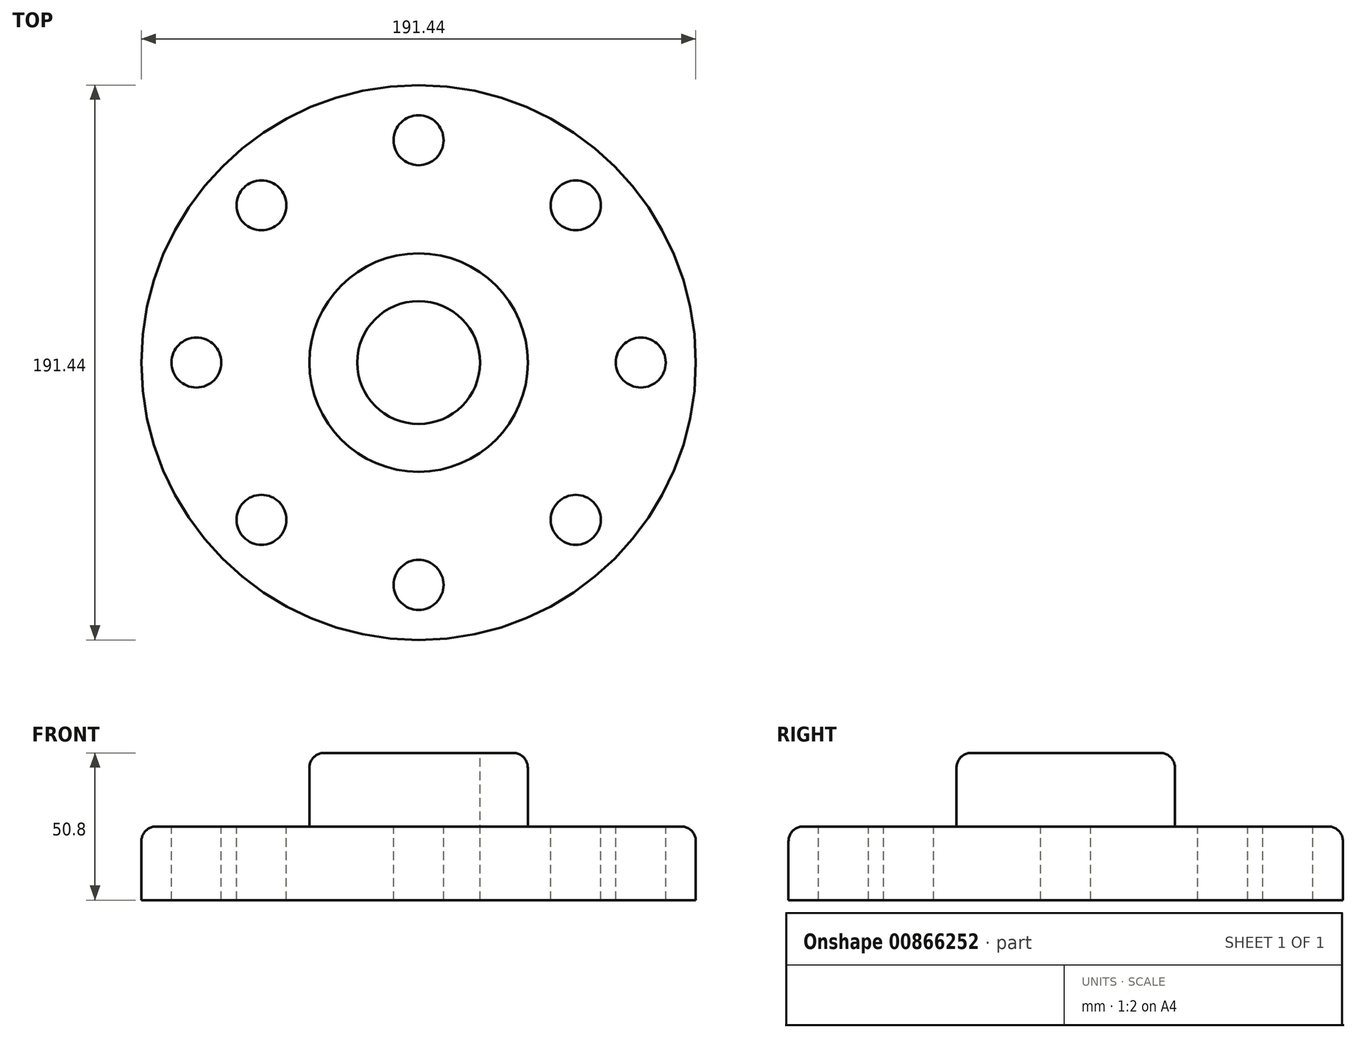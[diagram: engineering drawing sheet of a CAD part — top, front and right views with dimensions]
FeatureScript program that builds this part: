
annotation { "Feature Type Name" : "Feature", "Feature Type Description" : "" }
export const myFeature = defineFeature(function(context is Context, id is Id, definition is map)
    precondition{}
    {
        {
            var Q0;
            Q0=qCreatedBy(makeId("Top.planeOp"),FACE);
            var sketch = newSketch(context, id + "F0", { "sketchPlane" : qUnion([Q0])});
            skCircle(sketch, "E0", {"center": v(0, 0) * mm, "radius": 95.72 * mm});
            skCircle(sketch, "E1", {"center": v(0, 0) * mm, "radius": 37.7 * mm});
            skSolve(sketch);
        }
        {
            var Q0;
            Q0=makeQuery(id+"F0.imprint","IMPRINT",FACE,{"disambiguationData":[TD([[makeQuery(id+"F0.imprint","IMPRINT",EDGE,{"derivedFrom":sQuery(id+"F0.wireOp",EDGE,"E1")}),1.0]])]});
            extrude(context, id + "F1", {"entities" : qUnion([Q0]), "depth" : 50.8 * mm, "offsetDistance" : 25.4 * mm});
        }
        {
            var Q0;
            Q0 = qSketchRegion(id + "F0", true);
            extrude(context, id + "F2", {"entities" : qUnion([Q0]), "operationType" : NewBodyOperationType.ADD, "depth" : 25.4 * mm, "offsetDistance" : 25.4 * mm});
        }
        {
            var Q0;
            Q0=makeQuery(id+"F2.opExtrude","CAP_FACE",FACE,{"disambiguationData":[OSD([sQuery(id+"F0.wireOp",EDGE,"E0"),sQuery(id+"F0.wireOp",EDGE,"E1")])],"isStart":false});
            var sketch = newSketch(context, id + "F3", { "sketchPlane" : qUnion([Q0])});
            skLineSegment(sketch, "E2", {"start": v(0, 109.72) * mm, "end": v(0, 0) * mm, "construction": true});
            skLineSegment(sketch, "E3", {"start": v(0, 0) * mm, "end": v(-126.56, 0) * mm, "construction": true});
            skCircle(sketch, "E4", {"center": v(0, 76.73) * mm, "radius": 8.62 * mm});
            skCircle(sketch, "E5.1.0", {"center": v(-54.26, 54.26) * mm, "radius": 8.62 * mm});
            skCircle(sketch, "E5.2.0", {"center": v(-76.73, 0) * mm, "radius": 8.62 * mm});
            skCircle(sketch, "E5.3.0", {"center": v(-54.26, -54.26) * mm, "radius": 8.62 * mm});
            skCircle(sketch, "E5.4.0", {"center": v(0, -76.73) * mm, "radius": 8.62 * mm});
            skCircle(sketch, "E5.5.0", {"center": v(54.26, -54.26) * mm, "radius": 8.62 * mm});
            skCircle(sketch, "E5.6.0", {"center": v(76.73, 0) * mm, "radius": 8.62 * mm});
            skCircle(sketch, "E5.7.0", {"center": v(54.26, 54.26) * mm, "radius": 8.62 * mm});
            skPoint(sketch, "E5.center", {"position": v(0, 0) * mm});
            skSolve(sketch);
        }
        {
            var Q0;
            Q0=makeQuery(id+"F3.imprint","IMPRINT",FACE,{"disambiguationData":[TD([[makeQuery(id+"F3.imprint","IMPRINT",EDGE,{"derivedFrom":sQuery(id+"F3.wireOp",EDGE,"E4")}),1.0]])]});
            var Q1;
            Q1=makeQuery(id+"F3.imprint","IMPRINT",FACE,{"disambiguationData":[TD([[makeQuery(id+"F3.imprint","IMPRINT",EDGE,{"derivedFrom":sQuery(id+"F3.wireOp",EDGE,"E5.1.0")}),1.0]])]});
            var Q2;
            Q2=makeQuery(id+"F3.imprint","IMPRINT",FACE,{"disambiguationData":[TD([[makeQuery(id+"F3.imprint","IMPRINT",EDGE,{"derivedFrom":sQuery(id+"F3.wireOp",EDGE,"E5.2.0")}),1.0]])]});
            var Q3;
            Q3=makeQuery(id+"F3.imprint","IMPRINT",FACE,{"disambiguationData":[TD([[makeQuery(id+"F3.imprint","IMPRINT",EDGE,{"derivedFrom":sQuery(id+"F3.wireOp",EDGE,"E5.3.0")}),1.0]])]});
            var Q4;
            Q4=makeQuery(id+"F3.imprint","IMPRINT",FACE,{"disambiguationData":[TD([[makeQuery(id+"F3.imprint","IMPRINT",EDGE,{"derivedFrom":sQuery(id+"F3.wireOp",EDGE,"E5.4.0")}),1.0]])]});
            var Q5;
            Q5=makeQuery(id+"F3.imprint","IMPRINT",FACE,{"disambiguationData":[TD([[makeQuery(id+"F3.imprint","IMPRINT",EDGE,{"derivedFrom":sQuery(id+"F3.wireOp",EDGE,"E5.5.0")}),1.0]])]});
            var Q6;
            Q6=makeQuery(id+"F3.imprint","IMPRINT",FACE,{"disambiguationData":[TD([[makeQuery(id+"F3.imprint","IMPRINT",EDGE,{"derivedFrom":sQuery(id+"F3.wireOp",EDGE,"E5.6.0")}),1.0]])]});
            var Q7;
            Q7=makeQuery(id+"F3.imprint","IMPRINT",FACE,{"disambiguationData":[TD([[makeQuery(id+"F3.imprint","IMPRINT",EDGE,{"derivedFrom":sQuery(id+"F3.wireOp",EDGE,"E5.7.0")}),1.0]])]});
            extrude(context, id + "F4", {"entities" : qUnion([Q0, Q1, Q2, Q3, Q4, Q5, Q6, Q7]), "operationType" : NewBodyOperationType.REMOVE, "endBound" : BoundingType.THROUGH_ALL, "oppositeDirection" : true, "depth" : 25.4 * mm, "offsetDistance" : 25.4 * mm});
        }
        {
            var Q0;
            Q0=makeQuery(id+"F1.opExtrude","CAP_FACE",FACE,{"disambiguationData":[OSD([sQuery(id+"F0.wireOp",EDGE,"E1")])],"isStart":false});
            var sketch = newSketch(context, id + "F5", { "sketchPlane" : qUnion([Q0])});
            skCircle(sketch, "E6", {"center": v(0, 0) * mm, "radius": 21.22 * mm});
            skSolve(sketch);
        }
        {
            var Q0;
            Q0 = qSketchRegion(id + "F5", true);
            extrude(context, id + "F6", {"entities" : qUnion([Q0]), "operationType" : NewBodyOperationType.REMOVE, "endBound" : BoundingType.THROUGH_ALL, "oppositeDirection" : true, "depth" : 25.4 * mm, "offsetDistance" : 25.4 * mm});
        }
        {
            var Q0;
            Q0=makeQuery(id+"F2.opExtrude","CAP_EDGE",EDGE,{"disambiguationData":[OSD([sQuery(id+"F0.wireOp",EDGE,"E0")])],"isStart":false});
            var Q1;
            Q1=makeQuery(id+"F1.opExtrude","CAP_EDGE",EDGE,{"disambiguationData":[OSD([sQuery(id+"F0.wireOp",EDGE,"E1")])],"isStart":false});
            var Q2;
            Q2=makeQuery(id+"F6.boolean.opBoolean","COPY",EDGE,{"derivedFrom":makeQuery(id+"F6.opExtrude","CAP_EDGE",EDGE,{"disambiguationData":[OSD([sQuery(id+"F5.wireOp",EDGE,"E6")])],"isStart":true})});
            fillet(context, id + "F7", {"entities" : qUnion([Q0, Q1, Q2]), "radius" : 5.08 * mm, "tangentPropagation" : true, "allowEdgeOverflow" : false});
        }
    });
